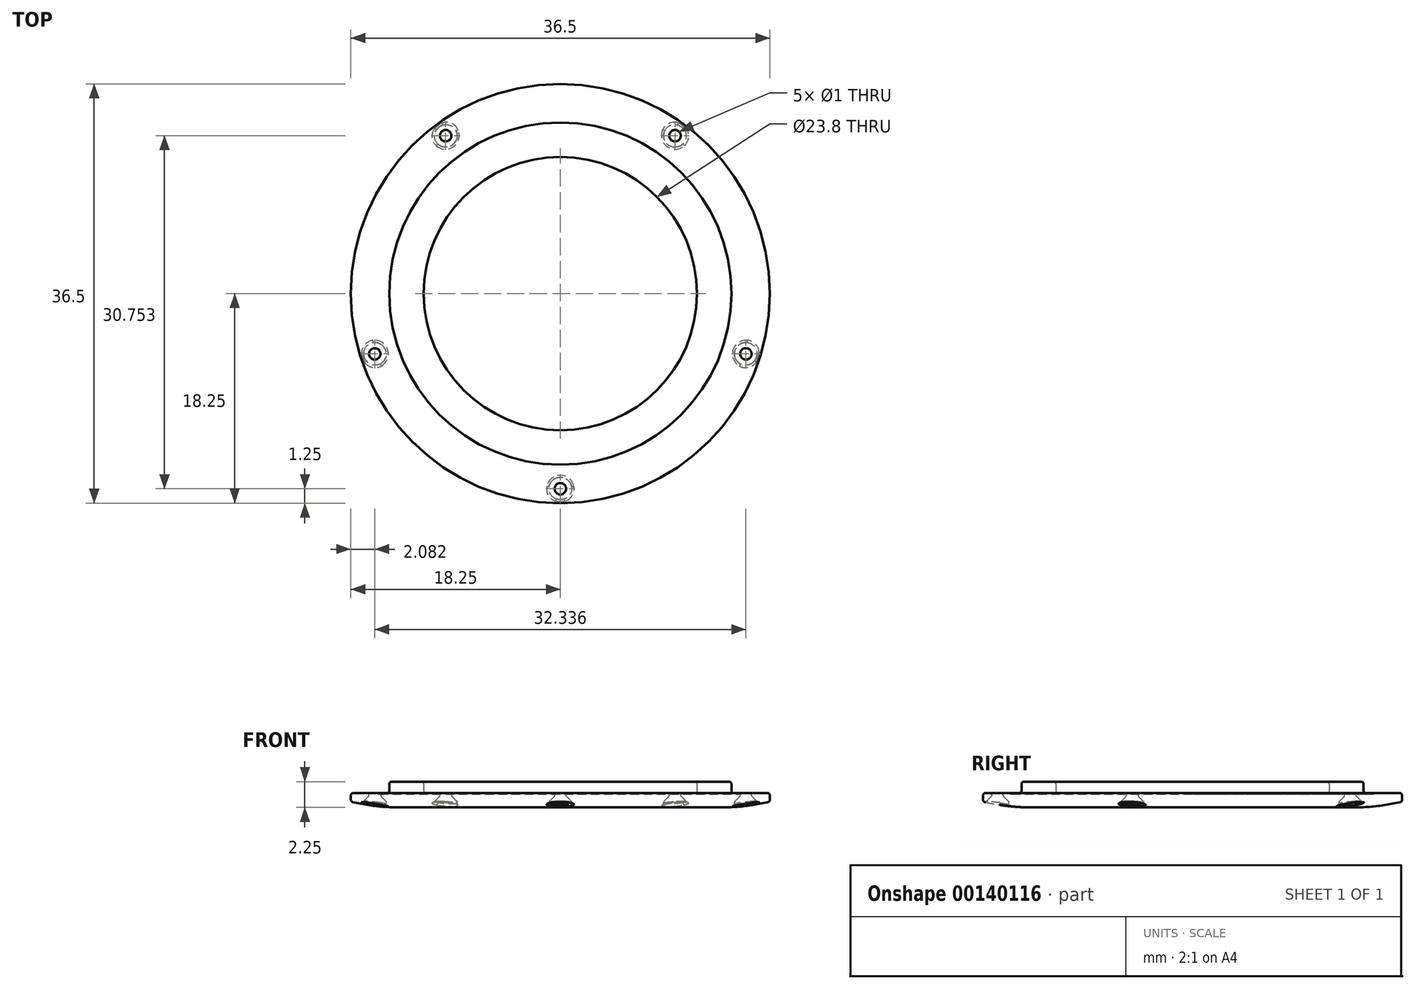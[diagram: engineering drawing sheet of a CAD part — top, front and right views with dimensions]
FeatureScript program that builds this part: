
annotation { "Feature Type Name" : "Feature", "Feature Type Description" : "" }
export const myFeature = defineFeature(function(context is Context, id is Id, definition is map)
    precondition{}
    {
        {
            var Q0;
            Q0=qCreatedBy(makeId("Front.planeOp"),FACE);
            var sketch = newSketch(context, id + "F0", { "sketchPlane" : qUnion([Q0])});
            skLineSegment(sketch, "E0", {"start": v(0, 0) * mm, "end": v(0, -1.25) * mm});
            skLineSegment(sketch, "E1", {"start": v(0, 0) * mm, "end": v(-11.7, 0) * mm});
            skLineSegment(sketch, "E2", {"start": v(-11.9, 0.2) * mm, "end": v(-11.9, 0.8) * mm});
            skLineSegment(sketch, "E3", {"start": v(-12.1, 1) * mm, "end": v(-14.7, 1) * mm});
            skLineSegment(sketch, "E4", {"start": v(-14.9, 0.8) * mm, "end": v(-14.9, 0.2) * mm});
            skLineSegment(sketch, "E5", {"start": v(-15.1, 0) * mm, "end": v(-15.47, 0) * mm});
            skLineSegment(sketch, "E6", {"start": v(-18.25, -0.2) * mm, "end": v(-18.25, -0.6) * mm});
            skLineSegment(sketch, "E7", {"start": v(-14, -1.25) * mm, "end": v(0, -1.25) * mm});
            skLineSegment(sketch, "E8", {"start": v(0, 0) * mm, "end": v(0, 1) * mm, "construction": true});
            skArc(sketch, "E9", {"start": v(-14, -1.25) * mm, "mid": v(-16.06, -1.13) * mm, "end": v(-18.1, -0.79) * mm});
            skPoint(sketch, "E10.visualSharp", {"position": v(-14.9, 0) * mm});
            skArc(sketch, "E10.filletArc", {"start": v(-15.1, 0) * mm, "mid": v(-14.96, 0.06) * mm, "end": v(-14.9, 0.2) * mm});
            skPoint(sketch, "E11.visualSharp", {"position": v(-14.9, 1) * mm});
            skArc(sketch, "E11.filletArc", {"start": v(-14.7, 1) * mm, "mid": v(-14.84, 0.94) * mm, "end": v(-14.9, 0.8) * mm});
            skPoint(sketch, "E12.visualSharp", {"position": v(-11.9, 0) * mm});
            skArc(sketch, "E12.filletArc", {"start": v(-11.9, 0.2) * mm, "mid": v(-11.84, 0.06) * mm, "end": v(-11.7, 0) * mm});
            skPoint(sketch, "E13.visualSharp", {"position": v(-18.25, 0) * mm});
            skArc(sketch, "E13.filletArc", {"start": v(-18.05, 0) * mm, "mid": v(-18.2, -0.06) * mm, "end": v(-18.25, -0.2) * mm});
            skPoint(sketch, "E14.visualSharp", {"position": v(-18.25, -0.75) * mm});
            skArc(sketch, "E14.filletArc", {"start": v(-18.25, -0.6) * mm, "mid": v(-18.2, -0.72) * mm, "end": v(-18.1, -0.79) * mm});
            skPoint(sketch, "E15.visualSharp", {"position": v(-11.9, 1) * mm});
            skArc(sketch, "E15.filletArc", {"start": v(-11.9, 0.8) * mm, "mid": v(-11.96, 0.94) * mm, "end": v(-12.1, 1) * mm});
            skPoint(sketch, "E16.visualSharp", {"position": v(0, -1.25) * mm});
            skArc(sketch, "E17", {"start": v(-15.9, -0.04) * mm, "mid": v(-15.75, -0.1) * mm, "end": v(-15.6, -0.04) * mm});
            skLineSegment(sketch, "E18.trimOffspring", {"start": v(-16.03, 0) * mm, "end": v(-18.05, 0) * mm});
            skPoint(sketch, "E19.visualSharp", {"position": v(-15.95, 0) * mm});
            skArc(sketch, "E19.filletArc", {"start": v(-15.9, -0.04) * mm, "mid": v(-15.97, -0.01) * mm, "end": v(-16.03, 0) * mm});
            skPoint(sketch, "E20.visualSharp", {"position": v(-15.55, 0) * mm});
            skArc(sketch, "E20.filletArc", {"start": v(-15.47, 0) * mm, "mid": v(-15.53, -0.01) * mm, "end": v(-15.6, -0.04) * mm});
            skSolve(sketch);
        }
        {
            var Q0;
            Q0 = qSketchRegion(id + "F0", true);
            var Q1;
            Q1=sQuery(id+"F0.wireOp",EDGE,"E8");
            revolve(context, id + "F1", {"entities" : qUnion([Q0]), "axis" : qUnion([Q1]), "revolveType" : RevolveType.FULL});
        }
        {
            var Q0;
            Q0=qCreatedBy(makeId("Right.planeOp"),FACE);
            var sketch = newSketch(context, id + "F2", { "sketchPlane" : qUnion([Q0])});
            skLineSegment(sketch, "E21", {"start": v(-17, 0) * mm, "end": v(-17.5, 0) * mm});
            skLineSegment(sketch, "E22", {"start": v(-17, -1.25) * mm, "end": v(-18, -1.25) * mm});
            skLineSegment(sketch, "E23", {"start": v(-18, -1.25) * mm, "end": v(-18, -0.75) * mm});
            skLineSegment(sketch, "E24", {"start": v(-17, 0) * mm, "end": v(-17, 0.93) * mm, "construction": true});
            skLineSegment(sketch, "E25", {"start": v(-17, 0) * mm, "end": v(-17, -1.25) * mm});
            skLineSegment(sketch, "E26", {"start": v(-17.5, 0) * mm, "end": v(-17.5, -0.25) * mm});
            skLineSegment(sketch, "E27", {"start": v(-17.5, -0.25) * mm, "end": v(-18, -0.75) * mm});
            skSolve(sketch);
        }
        {
            var Q0;
            Q0 = qSketchRegion(id + "F2", true);
            var Q1;
            Q1=makeQuery(id+"F2.imprint","IMPRINT",FACE,{"disambiguationData":[TD([[makeQuery(id+"F2.imprint","IMPRINT",EDGE,{"derivedFrom":sQuery(id+"F2.wireOp",EDGE,"E21")}),1.0]])]});
            var Q2;
            Q2=sQuery(id+"F2.wireOp",EDGE,"E24");
            revolve(context, id + "F3", {"entities" : qUnion([Q0, Q1]), "axis" : qUnion([Q2]), "revolveType" : RevolveType.FULL, "oppositeDirection" : true});
        }
        {
            var Q0;
            Q0=makeQuery(id+"F3.opRevolve","SWEPT_BODY",BODY,{"disambiguationData":[OSD([sQuery(id+"F2.wireOp",EDGE,"E21"),sQuery(id+"F2.wireOp",EDGE,"2oNXKCKB-Rh66-Nj45-adpD-4nFgSYGKnnpU"),sQuery(id+"F2.wireOp",EDGE,"E22"),sQuery(id+"F2.wireOp",EDGE,"E23"),sQuery(id+"F2.wireOp",EDGE,"tctMOU8y-Mgo1-Lk33-zD8C-WWPehcmeRYiv"),sQuery(id+"F2.wireOp",EDGE,"E25")])]});
            var Q1;
            Q1=makeQuery(id+"F1.opRevolve","SWEPT_EDGE",EDGE,{"disambiguationData":[OSD([sQuery(id+"F0.wireOp",EDGE,"E7"),sQuery(id+"F0.wireOp",EDGE,"E9")])]});
            circularPattern(context, id + "F4", {"operationType" : NewBodyOperationType.REMOVE, "entities" : qUnion([Q0]), "axis" : qUnion([Q1]), "angle" : 360 * degree, "instanceCount" : 5, "equalSpace" : true, "computeTransformsWithoutBuiltin" : true});
        }
        {
            var Q0;
            Q0=makeQuery(id+"F4.boolean.opBoolean","COPY",EDGE,{"derivedFrom":makeQuery(id+"F4.opPattern","COPY",EDGE,{"derivedFrom":makeQuery(id+"F3.opRevolve","SWEPT_EDGE",EDGE,{"disambiguationData":[OSD([sQuery(id+"F2.wireOp",EDGE,"E21"),sQuery(id+"F2.wireOp",EDGE,"tctMOU8y-Mgo1-Lk33-zD8C-WWPehcmeRYiv")])]}),"instanceName":"1"})});
            var Q1;
            Q1=makeQuery(id+"F4.boolean.opBoolean","COPY",EDGE,{"derivedFrom":makeQuery(id+"F3.opRevolve","SWEPT_EDGE",EDGE,{"disambiguationData":[OSD([sQuery(id+"F2.wireOp",EDGE,"E21"),sQuery(id+"F2.wireOp",EDGE,"tctMOU8y-Mgo1-Lk33-zD8C-WWPehcmeRYiv")])]})});
            var Q2;
            Q2=makeQuery(id+"F4.boolean.opBoolean","COPY",EDGE,{"derivedFrom":makeQuery(id+"F4.opPattern","COPY",EDGE,{"derivedFrom":makeQuery(id+"F3.opRevolve","SWEPT_EDGE",EDGE,{"disambiguationData":[OSD([sQuery(id+"F2.wireOp",EDGE,"E21"),sQuery(id+"F2.wireOp",EDGE,"tctMOU8y-Mgo1-Lk33-zD8C-WWPehcmeRYiv")])]}),"instanceName":"3"})});
            var Q3;
            Q3=makeQuery(id+"F4.boolean.opBoolean","COPY",EDGE,{"derivedFrom":makeQuery(id+"F4.opPattern","COPY",EDGE,{"derivedFrom":makeQuery(id+"F3.opRevolve","SWEPT_EDGE",EDGE,{"disambiguationData":[OSD([sQuery(id+"F2.wireOp",EDGE,"E21"),sQuery(id+"F2.wireOp",EDGE,"tctMOU8y-Mgo1-Lk33-zD8C-WWPehcmeRYiv")])]}),"instanceName":"2"})});
            var Q4;
            Q4=makeQuery(id+"F4.boolean.opBoolean","COPY",EDGE,{"derivedFrom":makeQuery(id+"F4.opPattern","COPY",EDGE,{"derivedFrom":makeQuery(id+"F3.opRevolve","SWEPT_EDGE",EDGE,{"disambiguationData":[OSD([sQuery(id+"F2.wireOp",EDGE,"E21"),sQuery(id+"F2.wireOp",EDGE,"tctMOU8y-Mgo1-Lk33-zD8C-WWPehcmeRYiv")])]}),"instanceName":"4"})});
            var Q5;
            Q5=makeQuery(id+"F4.boolean.opBoolean","COPY",EDGE,{"derivedFrom":makeQuery(id+"F3.opRevolve","SWEPT_EDGE",EDGE,{"disambiguationData":[OSD([sQuery(id+"F2.wireOp",EDGE,"E23"),sQuery(id+"F2.wireOp",EDGE,"E27")])]})});
            var Q6;
            Q6=makeQuery(id+"F4.boolean.opBoolean","COPY",EDGE,{"derivedFrom":makeQuery(id+"F4.opPattern","COPY",EDGE,{"derivedFrom":makeQuery(id+"F3.opRevolve","SWEPT_EDGE",EDGE,{"disambiguationData":[OSD([sQuery(id+"F2.wireOp",EDGE,"E23"),sQuery(id+"F2.wireOp",EDGE,"E27")])]}),"instanceName":"1"})});
            var Q7;
            Q7=makeQuery(id+"F4.boolean.opBoolean","COPY",EDGE,{"derivedFrom":makeQuery(id+"F4.opPattern","COPY",EDGE,{"derivedFrom":makeQuery(id+"F3.opRevolve","SWEPT_EDGE",EDGE,{"disambiguationData":[OSD([sQuery(id+"F2.wireOp",EDGE,"E23"),sQuery(id+"F2.wireOp",EDGE,"E27")])]}),"instanceName":"2"})});
            var Q8;
            Q8=makeQuery(id+"F4.boolean.opBoolean","COPY",EDGE,{"derivedFrom":makeQuery(id+"F4.opPattern","COPY",EDGE,{"derivedFrom":makeQuery(id+"F3.opRevolve","SWEPT_EDGE",EDGE,{"disambiguationData":[OSD([sQuery(id+"F2.wireOp",EDGE,"E23"),sQuery(id+"F2.wireOp",EDGE,"E27")])]}),"instanceName":"3"})});
            var Q9;
            Q9=makeQuery(id+"F4.boolean.opBoolean","COPY",EDGE,{"derivedFrom":makeQuery(id+"F4.opPattern","COPY",EDGE,{"derivedFrom":makeQuery(id+"F3.opRevolve","SWEPT_EDGE",EDGE,{"disambiguationData":[OSD([sQuery(id+"F2.wireOp",EDGE,"E23"),sQuery(id+"F2.wireOp",EDGE,"E27")])]}),"instanceName":"4"})});
            fillet(context, id + "F5", {"entities" : qUnion([Q0, Q1, Q2, Q3, Q4, Q5, Q6, Q7, Q8, Q9]), "radius" : 0.2 * mm, "tangentPropagation" : true, "allowEdgeOverflow" : false});
        }
        {
            var Q0;
            Q0=makeQuery(id+"F4.boolean.opBoolean","INTERSECT",EDGE,{"derivedFrom":[makeQuery(id+"F1.opRevolve","SWEPT_FACE",FACE,{"disambiguationData":[OSD([sQuery(id+"F0.wireOp",EDGE,"E9")])]}),makeQuery(id+"F3.opRevolve","SWEPT_FACE",FACE,{"disambiguationData":[OSD([sQuery(id+"F2.wireOp",EDGE,"E23")])]})]});
            var Q1;
            Q1=makeQuery(id+"F4.boolean.opBoolean","INTERSECT",EDGE,{"derivedFrom":[makeQuery(id+"F1.opRevolve","SWEPT_FACE",FACE,{"disambiguationData":[OSD([sQuery(id+"F0.wireOp",EDGE,"E9")])]}),makeQuery(id+"F4.opPattern","COPY",FACE,{"derivedFrom":makeQuery(id+"F3.opRevolve","SWEPT_FACE",FACE,{"disambiguationData":[OSD([sQuery(id+"F2.wireOp",EDGE,"E23")])]}),"instanceName":"1"})]});
            var Q2;
            Q2=makeQuery(id+"F4.boolean.opBoolean","INTERSECT",EDGE,{"derivedFrom":[makeQuery(id+"F1.opRevolve","SWEPT_FACE",FACE,{"disambiguationData":[OSD([sQuery(id+"F0.wireOp",EDGE,"E9")])]}),makeQuery(id+"F4.opPattern","COPY",FACE,{"derivedFrom":makeQuery(id+"F3.opRevolve","SWEPT_FACE",FACE,{"disambiguationData":[OSD([sQuery(id+"F2.wireOp",EDGE,"E23")])]}),"instanceName":"4"})]});
            var Q3;
            Q3=makeQuery(id+"F4.boolean.opBoolean","INTERSECT",EDGE,{"derivedFrom":[makeQuery(id+"F1.opRevolve","SWEPT_FACE",FACE,{"disambiguationData":[OSD([sQuery(id+"F0.wireOp",EDGE,"E9")])]}),makeQuery(id+"F4.opPattern","COPY",FACE,{"derivedFrom":makeQuery(id+"F3.opRevolve","SWEPT_FACE",FACE,{"disambiguationData":[OSD([sQuery(id+"F2.wireOp",EDGE,"E23")])]}),"instanceName":"2"})]});
            var Q4;
            Q4=makeQuery(id+"F4.boolean.opBoolean","INTERSECT",EDGE,{"derivedFrom":[makeQuery(id+"F1.opRevolve","SWEPT_FACE",FACE,{"disambiguationData":[OSD([sQuery(id+"F0.wireOp",EDGE,"E9")])]}),makeQuery(id+"F4.opPattern","COPY",FACE,{"derivedFrom":makeQuery(id+"F3.opRevolve","SWEPT_FACE",FACE,{"disambiguationData":[OSD([sQuery(id+"F2.wireOp",EDGE,"E23")])]}),"instanceName":"3"})]});
            var Q5;
            Q5=makeQuery(id+"F4.boolean.opBoolean","COPY",EDGE,{"derivedFrom":makeQuery(id+"F3.opRevolve","SWEPT_EDGE",EDGE,{"disambiguationData":[OSD([sQuery(id+"F2.wireOp",EDGE,"E26"),sQuery(id+"F2.wireOp",EDGE,"E27")])]})});
            var Q6;
            Q6=makeQuery(id+"F4.boolean.opBoolean","COPY",EDGE,{"derivedFrom":makeQuery(id+"F4.opPattern","COPY",EDGE,{"derivedFrom":makeQuery(id+"F3.opRevolve","SWEPT_EDGE",EDGE,{"disambiguationData":[OSD([sQuery(id+"F2.wireOp",EDGE,"E26"),sQuery(id+"F2.wireOp",EDGE,"E27")])]}),"instanceName":"1"})});
            var Q7;
            Q7=makeQuery(id+"F4.boolean.opBoolean","COPY",EDGE,{"derivedFrom":makeQuery(id+"F4.opPattern","COPY",EDGE,{"derivedFrom":makeQuery(id+"F3.opRevolve","SWEPT_EDGE",EDGE,{"disambiguationData":[OSD([sQuery(id+"F2.wireOp",EDGE,"E26"),sQuery(id+"F2.wireOp",EDGE,"E27")])]}),"instanceName":"2"})});
            var Q8;
            Q8=makeQuery(id+"F4.boolean.opBoolean","COPY",EDGE,{"derivedFrom":makeQuery(id+"F4.opPattern","COPY",EDGE,{"derivedFrom":makeQuery(id+"F3.opRevolve","SWEPT_EDGE",EDGE,{"disambiguationData":[OSD([sQuery(id+"F2.wireOp",EDGE,"E26"),sQuery(id+"F2.wireOp",EDGE,"E27")])]}),"instanceName":"3"})});
            var Q9;
            Q9=makeQuery(id+"F4.boolean.opBoolean","COPY",EDGE,{"derivedFrom":makeQuery(id+"F4.opPattern","COPY",EDGE,{"derivedFrom":makeQuery(id+"F3.opRevolve","SWEPT_EDGE",EDGE,{"disambiguationData":[OSD([sQuery(id+"F2.wireOp",EDGE,"E26"),sQuery(id+"F2.wireOp",EDGE,"E27")])]}),"instanceName":"4"})});
            fillet(context, id + "F6", {"entities" : qUnion([Q0, Q1, Q2, Q3, Q4, Q5, Q6, Q7, Q8, Q9]), "radius" : 0.2 * mm, "tangentPropagation" : true, "allowEdgeOverflow" : false});
        }
    });
